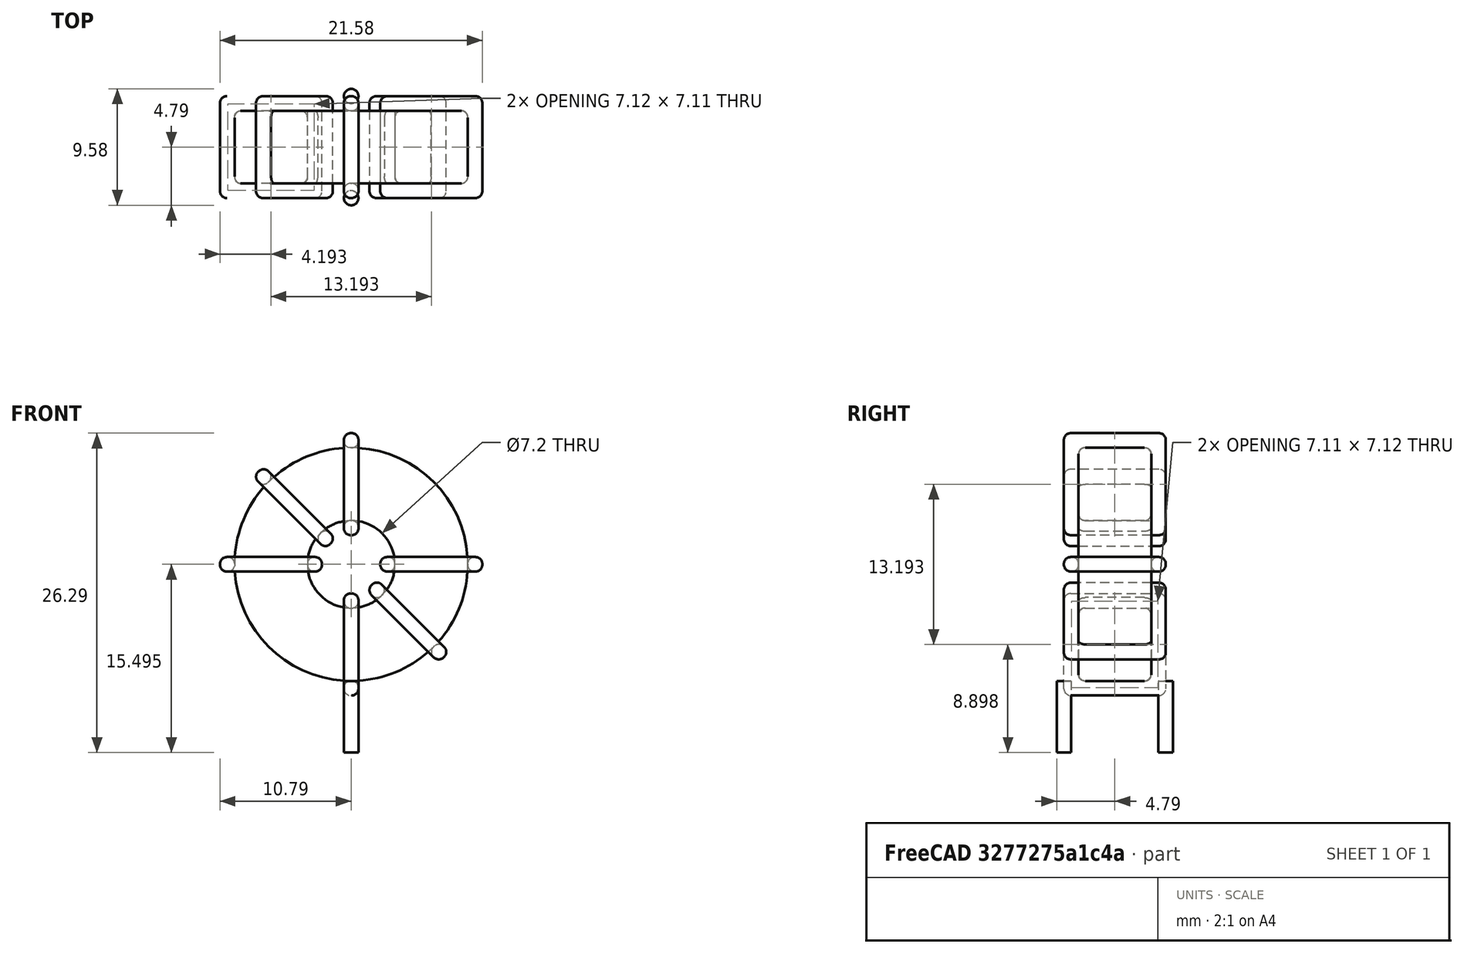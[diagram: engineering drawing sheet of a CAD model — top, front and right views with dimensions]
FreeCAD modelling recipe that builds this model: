
FCSTD DOCUMENT  (FreeCAD 0.16R6703 (Git))
Label: L_Toroid_Vertical_L21.6mm_W8.4mm_P8.38mm_Pulse_G
License: All rights reserved
LicenseURL: http://en.wikipedia.org/wiki/All_rights_reserved
objects: Sketcher::SketchObject×6, PartDesign::Pad×6, PartDesign::Fillet×5, Spreadsheet::Sheet×1
note: 23 computed .brp shape members not serialized (recipe doc carries the construction recipe); baked Part::Feature solids carry a one-line shape summary decoded from their .brp

FEATURE [Spreadsheet::Sheet] Spreadsheet  label="dimensions"
  cells = A1=Wx; B1(Wx)=21.59; C1(WW)=7.196666666666666; D1=21.59; A2=Wy; B2(Wy)=8.380000000000001; D2=8.380000000000001; A3=RM; B3(RMx)=8.380000000000001; C3(RMy)=0; A4=d_wire; B4(d_wire)=1.2; A5=H; B5(H)=21.59; A6=offsetx; B6(offsetx)=10.795
FEATURE [Sketcher::SketchObject] Sketch
  Placement = pos=(0,-4.19,0) rot=(1,0,0;1.5708rad)
  expr: Placement.Base.y = -Spreadsheet.RMx / 2
  expr: Constraints[0] = Spreadsheet.Wx / 2 - Spreadsheet.d_wire
  expr: Constraints[4] = Spreadsheet.WW / 2
  expr: Constraints[2] = Spreadsheet.Wx / 2 + Spreadsheet.d_wire + 0.5
  sketch-geometry (2):
    g0: Circle CenterX=0 CenterY=12.495 CenterZ=0 NormalX=0 NormalY=0 NormalZ=1 Radius=9.595
    g1: Circle CenterX=0 CenterY=12.495 CenterZ=0 NormalX=0 NormalY=0 NormalZ=1 Radius=3.59833
  constraints (5):
    c: Radius(g0) = 9.595
    c: DistanceX(g-1,g0) = 0
    c: DistanceY(g-1,g0) = 12.495
    c: Coincident(g1,g0)
    c: Radius(g1) = 3.59833
FEATURE [PartDesign::Pad] Pad
  Length = 5.98
  Length2 = 100
  Midplane = true
  Placement = pos=(0,-4.19,0) rot=(1,0,0;1.5708rad)
  Sketch = -> Sketch
  Type = 0
  expr: Length = Spreadsheet.Wy - 2 * Spreadsheet.d_wire
FEATURE [Sketcher::SketchObject] Sketch001
  Placement = pos=(0,0,1.7) rot=(0,0,1;0rad)
  expr: Placement.Base.z = 0.5 + Spreadsheet.d_wire
  expr: Constraints[4] = Spreadsheet.RMy
  expr: Constraints[2] = -Spreadsheet.RMx
  expr: Constraints[1] = Spreadsheet.d_wire / 2
  sketch-geometry (2):
    g0: Circle CenterX=0 CenterY=0 CenterZ=0 NormalX=0 NormalY=0 NormalZ=1 Radius=0.6
    g1: Circle CenterX=0 CenterY=-8.38 CenterZ=0 NormalX=0 NormalY=0 NormalZ=1 Radius=0.6
  constraints (5):
    c: Equal(g0,g1)
    c: Radius(g0) = 0.6
    c: DistanceY(g-1,g1) = -8.38
    c: Coincident(g0,g-1)
    c: DistanceX(g-1,g1) = 0
FEATURE [PartDesign::Pad] Pad001
  Length = 1.2
  Length2 = 4.7
  Placement = pos=(0,0,1.7) rot=(0,0,1;0rad)
  Reversed = true
  Sketch = -> Sketch001
  Type = 4
  expr: Length2 = 3.5 + Spreadsheet.d_wire
  expr: Length = Spreadsheet.d_wire
FEATURE [PartDesign::Fillet] Fillet
  Base = -> Pad [Edge6,Edge3,Edge2]
  Placement = pos=(0,-4.19,0) rot=(1,0,0;1.5708rad)
  Radius = 0.5
FEATURE [Sketcher::SketchObject] Sketch003
  Placement = pos=(0,0,12.495) rot=(1,0,0;3.14159rad)
  expr: Constraints[18] = Spreadsheet.d_wire
  expr: Constraints[16] = Spreadsheet.d_wire
  expr: Constraints[19] = Spreadsheet.d_wire
  expr: Constraints[17] = Spreadsheet.d_wire
  expr: Placement.Base.y = -1 * (Spreadsheet.RMx - Spreadsheet.Wy) / 2
  expr: Constraints[21] = (Spreadsheet.Wx - Spreadsheet.WW) / 2 - Spreadsheet.d_wire
  expr: Constraints[22] = Spreadsheet.Wx / 2 - Spreadsheet.d_wire
  expr: Constraints[43] = Spreadsheet.d_wire
  expr: Constraints[48] = Spreadsheet.Wx - Spreadsheet.d_wire * 2
  expr: Constraints[49] = Spreadsheet.Wy
  expr: Placement.Base.z = Spreadsheet.Wx / 2 + Spreadsheet.d_wire + 0.5
  sketch-geometry (16):
    g0: LineSegment StartX=-2.39833 StartY=0 StartZ=0 EndX=-10.795 EndY=0 EndZ=0
    g1: LineSegment StartX=-10.795 StartY=0 StartZ=0 EndX=-10.795 EndY=8.38 EndZ=0
    g2: LineSegment StartX=-10.795 StartY=8.38 StartZ=0 EndX=-2.39833 EndY=8.38 EndZ=0
    g3: LineSegment StartX=-2.39833 StartY=8.38 StartZ=0 EndX=-2.39833 EndY=0 EndZ=0
    g4: LineSegment StartX=-9.595 StartY=7.18 StartZ=0 EndX=-3.59833 EndY=7.18 EndZ=0
    g5: LineSegment StartX=-3.59833 StartY=7.18 StartZ=0 EndX=-3.59833 EndY=1.2 EndZ=0
    g6: LineSegment StartX=-3.59833 StartY=1.2 StartZ=0 EndX=-9.595 EndY=1.2 EndZ=0
    g7: LineSegment StartX=-9.595 StartY=1.2 StartZ=0 EndX=-9.595 EndY=7.18 EndZ=0
    g8: LineSegment StartX=2.39833 StartY=8.38 StartZ=0 EndX=10.795 EndY=8.38 EndZ=0
    g9: LineSegment StartX=10.795 StartY=8.38 StartZ=0 EndX=10.795 EndY=0 EndZ=0
    g10: LineSegment StartX=10.795 StartY=0 StartZ=0 EndX=2.39833 EndY=0 EndZ=0
    g11: LineSegment StartX=2.39833 StartY=0 StartZ=0 EndX=2.39833 EndY=8.38 EndZ=0
    g12: LineSegment StartX=3.59833 StartY=7.18 StartZ=0 EndX=9.595 EndY=7.18 EndZ=0
    g13: LineSegment StartX=9.595 StartY=7.18 StartZ=0 EndX=9.595 EndY=1.2 EndZ=0
    g14: LineSegment StartX=9.595 StartY=1.2 StartZ=0 EndX=3.59833 EndY=1.2 EndZ=0
    g15: LineSegment StartX=3.59833 StartY=1.2 StartZ=0 EndX=3.59833 EndY=7.18 EndZ=0
  constraints (50):
    c: Horizontal(g0)
    c: Coincident(g1,g0)
    c: Vertical(g1)
    c: Coincident(g2,g1)
    c: Horizontal(g2)
    c: Coincident(g3,g2)
    c: Coincident(g3,g0)
    c: Vertical(g3)
    c: Coincident(g4,g5)
    c: Coincident(g5,g6)
    c: Coincident(g6,g7)
    c: Coincident(g7,g4)
    c: Horizontal(g4)
    c: Horizontal(g6)
    c: Vertical(g5)
    c: Vertical(g7)
    c: DistanceX(g1,g4) = 1.2
    c: DistanceY(g4,g1) = 1.2
    c: DistanceX(g5,g0) = 1.2
    c: DistanceY(g0,g5) = 1.2
    c: DistanceY(g-1,g0) = 0
    c: DistanceX(g6,g6) = 5.99667
    c: DistanceX(g6,g-1) = 9.595
    c: Coincident(g8,g9)
    c: Coincident(g9,g10)
    c: Coincident(g10,g11)
    c: Coincident(g11,g8)
    c: Horizontal(g8)
    c: Horizontal(g10)
    c: Vertical(g9)
    c: Vertical(g11)
    c: Coincident(g12,g13)
    c: Coincident(g13,g14)
    c: Coincident(g14,g15)
    c: Coincident(g15,g12)
    c: Horizontal(g12)
    c: Horizontal(g14)
    c: Vertical(g13)
    c: Vertical(g15)
    c: DistanceY(g8,g2) = 0
    c: DistanceY(g10,g0) = 0
    c: DistanceY(g14,g5) = 0
    c: DistanceY(g12,g4) = 0
    c: DistanceX(g8,g12) = 1.2
    c: Equal(g8,g2)
    c: Equal(g12,g4)
    c: Equal(g9,g1)
    c: Equal(g13,g7)
    c: DistanceX(g4,g12) = 19.19
    c: DistanceY(g0,g1) = 8.38
FEATURE [PartDesign::Pad] Pad002
  Length = 1.2
  Length2 = 100
  Midplane = true
  Placement = pos=(0,0,12.495) rot=(1,0,0;3.14159rad)
  Sketch = -> Sketch003
  Type = 0
  expr: Length = Spreadsheet.d_wire
FEATURE [PartDesign::Fillet] Fillet001
  Base = -> Pad002 [Edge38,Edge41,Edge42,Edge43,Edge29,Edge32,Edge33,Edge34,Edge25,Edge35,Edge36,Edge13,Edge14,Edge15,Edge16,Edge17,Edge18,Edge19,Edge1,Edge2,Edge3,Edge4,Edge5,Edge6,Edge7,Edge37,Edge39,Edge40,Edge20,Edge23,Edge24,Edge21,Edge22,Edge8,Edge9,Edge10,Edge11,Edge12,Edge26,Edge27,+8 more]
  Placement = pos=(0,0,12.495) rot=(1,0,0;3.14159rad)
  Radius = 0.564
  expr: Radius = Spreadsheet.d_wire * 0.47
FEATURE [Sketcher::SketchObject] Sketch004
  Placement = pos=(0,0,12.495) rot=(0.92388,0,0.382683;3.14159rad)
  expr: Constraints[18] = Spreadsheet.d_wire
  expr: Constraints[16] = Spreadsheet.d_wire
  expr: Constraints[19] = Spreadsheet.d_wire
  expr: Constraints[17] = Spreadsheet.d_wire
  expr: Placement.Base.y = -1 * (Spreadsheet.RMx - Spreadsheet.Wy) / 2
  expr: Constraints[21] = (Spreadsheet.Wx - Spreadsheet.WW) / 2 - Spreadsheet.d_wire
  expr: Constraints[22] = Spreadsheet.Wx / 2 - Spreadsheet.d_wire
  expr: Constraints[43] = Spreadsheet.d_wire
  expr: Constraints[48] = Spreadsheet.Wx - 2 * Spreadsheet.d_wire
  expr: Constraints[49] = Spreadsheet.Wy
  expr: Placement.Base.z = Spreadsheet.Wx / 2 + Spreadsheet.d_wire + 0.5
  sketch-geometry (16):
    g0: LineSegment StartX=-2.39833 StartY=0 StartZ=0 EndX=-10.795 EndY=0 EndZ=0
    g1: LineSegment StartX=-10.795 StartY=0 StartZ=0 EndX=-10.795 EndY=8.38 EndZ=0
    g2: LineSegment StartX=-10.795 StartY=8.38 StartZ=0 EndX=-2.39833 EndY=8.38 EndZ=0
    g3: LineSegment StartX=-2.39833 StartY=8.38 StartZ=0 EndX=-2.39833 EndY=0 EndZ=0
    g4: LineSegment StartX=-9.595 StartY=7.18 StartZ=0 EndX=-3.59833 EndY=7.18 EndZ=0
    g5: LineSegment StartX=-3.59833 StartY=7.18 StartZ=0 EndX=-3.59833 EndY=1.2 EndZ=0
    g6: LineSegment StartX=-3.59833 StartY=1.2 StartZ=0 EndX=-9.595 EndY=1.2 EndZ=0
    g7: LineSegment StartX=-9.595 StartY=1.2 StartZ=0 EndX=-9.595 EndY=7.18 EndZ=0
    g8: LineSegment StartX=2.39833 StartY=8.38 StartZ=0 EndX=10.795 EndY=8.38 EndZ=0
    g9: LineSegment StartX=10.795 StartY=8.38 StartZ=0 EndX=10.795 EndY=0 EndZ=0
    g10: LineSegment StartX=10.795 StartY=0 StartZ=0 EndX=2.39833 EndY=0 EndZ=0
    g11: LineSegment StartX=2.39833 StartY=0 StartZ=0 EndX=2.39833 EndY=8.38 EndZ=0
    g12: LineSegment StartX=3.59833 StartY=7.18 StartZ=0 EndX=9.595 EndY=7.18 EndZ=0
    g13: LineSegment StartX=9.595 StartY=7.18 StartZ=0 EndX=9.595 EndY=1.2 EndZ=0
    g14: LineSegment StartX=9.595 StartY=1.2 StartZ=0 EndX=3.59833 EndY=1.2 EndZ=0
    g15: LineSegment StartX=3.59833 StartY=1.2 StartZ=0 EndX=3.59833 EndY=7.18 EndZ=0
  constraints (50):
    c: Horizontal(g0)
    c: Coincident(g1,g0)
    c: Vertical(g1)
    c: Coincident(g2,g1)
    c: Horizontal(g2)
    c: Coincident(g3,g2)
    c: Coincident(g3,g0)
    c: Vertical(g3)
    c: Coincident(g4,g5)
    c: Coincident(g5,g6)
    c: Coincident(g6,g7)
    c: Coincident(g7,g4)
    c: Horizontal(g4)
    c: Horizontal(g6)
    c: Vertical(g5)
    c: Vertical(g7)
    c: DistanceX(g1,g4) = 1.2
    c: DistanceY(g4,g1) = 1.2
    c: DistanceX(g5,g0) = 1.2
    c: DistanceY(g0,g5) = 1.2
    c: DistanceY(g-1,g0) = 0
    c: DistanceX(g6,g6) = 5.99667
    c: DistanceX(g6,g-1) = 9.595
    c: Coincident(g8,g9)
    c: Coincident(g9,g10)
    c: Coincident(g10,g11)
    c: Coincident(g11,g8)
    c: Horizontal(g8)
    c: Horizontal(g10)
    c: Vertical(g9)
    c: Vertical(g11)
    c: Coincident(g12,g13)
    c: Coincident(g13,g14)
    c: Coincident(g14,g15)
    c: Coincident(g15,g12)
    c: Horizontal(g12)
    c: Horizontal(g14)
    c: Vertical(g13)
    c: Vertical(g15)
    c: DistanceY(g8,g2) = 0
    c: DistanceY(g10,g0) = 0
    c: DistanceY(g14,g5) = 0
    c: DistanceY(g12,g4) = 0
    c: DistanceX(g8,g12) = 1.2
    c: Equal(g8,g2)
    c: Equal(g12,g4)
    c: Equal(g9,g1)
    c: Equal(g13,g7)
    c: DistanceX(g4,g12) = 19.19
    c: DistanceY(g0,g1) = 8.38
FEATURE [PartDesign::Pad] Pad003
  Length = 1.2
  Length2 = 100
  Midplane = true
  Placement = pos=(0,0,12.495) rot=(0.92388,0,0.382683;3.14159rad)
  Sketch = -> Sketch004
  Type = 0
  expr: Length = Spreadsheet.d_wire
FEATURE [PartDesign::Fillet] Fillet002
  Base = -> Pad003 [Edge38,Edge41,Edge42,Edge43,Edge29,Edge32,Edge33,Edge34,Edge25,Edge35,Edge36,Edge13,Edge14,Edge15,Edge16,Edge17,Edge18,Edge19,Edge1,Edge2,Edge3,Edge4,Edge5,Edge6,Edge7,Edge37,Edge39,Edge40,Edge20,Edge23,Edge24,Edge21,Edge22,Edge8,Edge9,Edge10,Edge11,Edge12,Edge26,Edge27,+8 more]
  Placement = pos=(0,0,12.495) rot=(0.92388,0,0.382683;3.14159rad)
  Radius = 0.564
  expr: Radius = Spreadsheet.d_wire * 0.47
FEATURE [Sketcher::SketchObject] Sketch005
  Placement = pos=(0,0,12.495) rot=(0.92388,0,-0.382683;3.14159rad)
  expr: Constraints[18] = Spreadsheet.d_wire
  expr: Constraints[16] = Spreadsheet.d_wire
  expr: Constraints[19] = Spreadsheet.d_wire
  expr: Constraints[17] = Spreadsheet.d_wire
  expr: Placement.Base.y = -1 * (Spreadsheet.RMx - Spreadsheet.Wy) / 2
  expr: Constraints[21] = (Spreadsheet.Wx - Spreadsheet.WW) / 2 - Spreadsheet.d_wire
  expr: Constraints[22] = Spreadsheet.Wx / 2 - Spreadsheet.d_wire
  expr: Constraints[43] = Spreadsheet.d_wire
  expr: Constraints[48] = Spreadsheet.Wx - 2 * Spreadsheet.d_wire
  expr: Constraints[49] = Spreadsheet.Wy
  expr: Placement.Base.z = Spreadsheet.Wx / 2 + Spreadsheet.d_wire + 0.5
  sketch-geometry (16):
    g0: LineSegment StartX=-2.39833 StartY=0 StartZ=0 EndX=-10.795 EndY=0 EndZ=0
    g1: LineSegment StartX=-10.795 StartY=0 StartZ=0 EndX=-10.795 EndY=8.38 EndZ=0
    g2: LineSegment StartX=-10.795 StartY=8.38 StartZ=0 EndX=-2.39833 EndY=8.38 EndZ=0
    g3: LineSegment StartX=-2.39833 StartY=8.38 StartZ=0 EndX=-2.39833 EndY=0 EndZ=0
    g4: LineSegment StartX=-9.595 StartY=7.18 StartZ=0 EndX=-3.59833 EndY=7.18 EndZ=0
    g5: LineSegment StartX=-3.59833 StartY=7.18 StartZ=0 EndX=-3.59833 EndY=1.2 EndZ=0
    g6: LineSegment StartX=-3.59833 StartY=1.2 StartZ=0 EndX=-9.595 EndY=1.2 EndZ=0
    g7: LineSegment StartX=-9.595 StartY=1.2 StartZ=0 EndX=-9.595 EndY=7.18 EndZ=0
    g8: LineSegment StartX=2.39833 StartY=8.38 StartZ=0 EndX=10.795 EndY=8.38 EndZ=0
    g9: LineSegment StartX=10.795 StartY=8.38 StartZ=0 EndX=10.795 EndY=0 EndZ=0
    g10: LineSegment StartX=10.795 StartY=0 StartZ=0 EndX=2.39833 EndY=0 EndZ=0
    g11: LineSegment StartX=2.39833 StartY=0 StartZ=0 EndX=2.39833 EndY=8.38 EndZ=0
    g12: LineSegment StartX=3.59833 StartY=7.18 StartZ=0 EndX=9.595 EndY=7.18 EndZ=0
    g13: LineSegment StartX=9.595 StartY=7.18 StartZ=0 EndX=9.595 EndY=1.2 EndZ=0
    g14: LineSegment StartX=9.595 StartY=1.2 StartZ=0 EndX=3.59833 EndY=1.2 EndZ=0
    g15: LineSegment StartX=3.59833 StartY=1.2 StartZ=0 EndX=3.59833 EndY=7.18 EndZ=0
  constraints (50):
    c: Horizontal(g0)
    c: Coincident(g1,g0)
    c: Vertical(g1)
    c: Coincident(g2,g1)
    c: Horizontal(g2)
    c: Coincident(g3,g2)
    c: Coincident(g3,g0)
    c: Vertical(g3)
    c: Coincident(g4,g5)
    c: Coincident(g5,g6)
    c: Coincident(g6,g7)
    c: Coincident(g7,g4)
    c: Horizontal(g4)
    c: Horizontal(g6)
    c: Vertical(g5)
    c: Vertical(g7)
    c: DistanceX(g1,g4) = 1.2
    c: DistanceY(g4,g1) = 1.2
    c: DistanceX(g5,g0) = 1.2
    c: DistanceY(g0,g5) = 1.2
    c: DistanceY(g-1,g0) = 0
    c: DistanceX(g6,g6) = 5.99667
    c: DistanceX(g6,g-1) = 9.595
    c: Coincident(g8,g9)
    c: Coincident(g9,g10)
    c: Coincident(g10,g11)
    c: Coincident(g11,g8)
    c: Horizontal(g8)
    c: Horizontal(g10)
    c: Vertical(g9)
    c: Vertical(g11)
    c: Coincident(g12,g13)
    c: Coincident(g13,g14)
    c: Coincident(g14,g15)
    c: Coincident(g15,g12)
    c: Horizontal(g12)
    c: Horizontal(g14)
    c: Vertical(g13)
    c: Vertical(g15)
    c: DistanceY(g8,g2) = 0
    c: DistanceY(g10,g0) = 0
    c: DistanceY(g14,g5) = 0
    c: DistanceY(g12,g4) = 0
    c: DistanceX(g8,g12) = 1.2
    c: Equal(g8,g2)
    c: Equal(g12,g4)
    c: Equal(g9,g1)
    c: Equal(g13,g7)
    c: DistanceX(g4,g12) = 19.19
    c: DistanceY(g0,g1) = 8.38
FEATURE [PartDesign::Pad] Pad004
  Length = 1.2
  Length2 = 100
  Midplane = true
  Placement = pos=(0,0,12.495) rot=(0.92388,0,-0.382683;3.14159rad)
  Sketch = -> Sketch005
  Type = 0
  expr: Length = Spreadsheet.d_wire
FEATURE [PartDesign::Fillet] Fillet003
  Base = -> Pad004 [Edge38,Edge41,Edge42,Edge43,Edge29,Edge32,Edge33,Edge34,Edge25,Edge35,Edge36,Edge13,Edge14,Edge15,Edge16,Edge17,Edge18,Edge19,Edge1,Edge2,Edge3,Edge4,Edge5,Edge6,Edge7,Edge37,Edge39,Edge40,Edge20,Edge23,Edge24,Edge21,Edge22,Edge8,Edge9,Edge10,Edge11,Edge12,Edge26,Edge27,+8 more]
  Placement = pos=(0,0,12.495) rot=(0.92388,0,-0.382683;3.14159rad)
  Radius = 0.564
  expr: Radius = Spreadsheet.d_wire * 0.47
FEATURE [Sketcher::SketchObject] Sketch006
  Placement = pos=(0,0,12.495) rot=(0.707107,0,0.707107;3.14159rad)
  expr: Constraints[18] = Spreadsheet.d_wire
  expr: Constraints[16] = Spreadsheet.d_wire
  expr: Constraints[19] = Spreadsheet.d_wire
  expr: Constraints[17] = Spreadsheet.d_wire
  expr: Placement.Base.y = -1 * (Spreadsheet.RMx - Spreadsheet.Wy) / 2
  expr: Constraints[21] = (Spreadsheet.Wx - Spreadsheet.WW) / 2 - Spreadsheet.d_wire
  expr: Constraints[22] = Spreadsheet.Wx / 2 - Spreadsheet.d_wire
  expr: Constraints[43] = Spreadsheet.d_wire
  expr: Constraints[48] = Spreadsheet.Wx - Spreadsheet.d_wire * 2
  expr: Constraints[49] = Spreadsheet.Wy
  expr: Placement.Base.z = Spreadsheet.Wx / 2 + Spreadsheet.d_wire + 0.5
  sketch-geometry (16):
    g0: LineSegment StartX=-2.39833 StartY=0 StartZ=0 EndX=-10.795 EndY=0 EndZ=0
    g1: LineSegment StartX=-10.795 StartY=0 StartZ=0 EndX=-10.795 EndY=8.38 EndZ=0
    g2: LineSegment StartX=-10.795 StartY=8.38 StartZ=0 EndX=-2.39833 EndY=8.38 EndZ=0
    g3: LineSegment StartX=-2.39833 StartY=8.38 StartZ=0 EndX=-2.39833 EndY=0 EndZ=0
    g4: LineSegment StartX=-9.595 StartY=7.18 StartZ=0 EndX=-3.59833 EndY=7.18 EndZ=0
    g5: LineSegment StartX=-3.59833 StartY=7.18 StartZ=0 EndX=-3.59833 EndY=1.2 EndZ=0
    g6: LineSegment StartX=-3.59833 StartY=1.2 StartZ=0 EndX=-9.595 EndY=1.2 EndZ=0
    g7: LineSegment StartX=-9.595 StartY=1.2 StartZ=0 EndX=-9.595 EndY=7.18 EndZ=0
    g8: LineSegment StartX=2.39833 StartY=8.38 StartZ=0 EndX=10.795 EndY=8.38 EndZ=0
    g9: LineSegment StartX=10.795 StartY=8.38 StartZ=0 EndX=10.795 EndY=0 EndZ=0
    g10: LineSegment StartX=10.795 StartY=0 StartZ=0 EndX=2.39833 EndY=0 EndZ=0
    g11: LineSegment StartX=2.39833 StartY=0 StartZ=0 EndX=2.39833 EndY=8.38 EndZ=0
    g12: LineSegment StartX=3.59833 StartY=7.18 StartZ=0 EndX=9.595 EndY=7.18 EndZ=0
    g13: LineSegment StartX=9.595 StartY=7.18 StartZ=0 EndX=9.595 EndY=1.2 EndZ=0
    g14: LineSegment StartX=9.595 StartY=1.2 StartZ=0 EndX=3.59833 EndY=1.2 EndZ=0
    g15: LineSegment StartX=3.59833 StartY=1.2 StartZ=0 EndX=3.59833 EndY=7.18 EndZ=0
  constraints (50):
    c: Horizontal(g0)
    c: Coincident(g1,g0)
    c: Vertical(g1)
    c: Coincident(g2,g1)
    c: Horizontal(g2)
    c: Coincident(g3,g2)
    c: Coincident(g3,g0)
    c: Vertical(g3)
    c: Coincident(g4,g5)
    c: Coincident(g5,g6)
    c: Coincident(g6,g7)
    c: Coincident(g7,g4)
    c: Horizontal(g4)
    c: Horizontal(g6)
    c: Vertical(g5)
    c: Vertical(g7)
    c: DistanceX(g1,g4) = 1.2
    c: DistanceY(g4,g1) = 1.2
    c: DistanceX(g5,g0) = 1.2
    c: DistanceY(g0,g5) = 1.2
    c: DistanceY(g-1,g0) = 0
    c: DistanceX(g6,g6) = 5.99667
    c: DistanceX(g6,g-1) = 9.595
    c: Coincident(g8,g9)
    c: Coincident(g9,g10)
    c: Coincident(g10,g11)
    c: Coincident(g11,g8)
    c: Horizontal(g8)
    c: Horizontal(g10)
    c: Vertical(g9)
    c: Vertical(g11)
    c: Coincident(g12,g13)
    c: Coincident(g13,g14)
    c: Coincident(g14,g15)
    c: Coincident(g15,g12)
    c: Horizontal(g12)
    c: Horizontal(g14)
    c: Vertical(g13)
    c: Vertical(g15)
    c: DistanceY(g8,g2) = 0
    c: DistanceY(g10,g0) = 0
    c: DistanceY(g14,g5) = 0
    c: DistanceY(g12,g4) = 0
    c: DistanceX(g8,g12) = 1.2
    c: Equal(g8,g2)
    c: Equal(g12,g4)
    c: Equal(g9,g1)
    c: Equal(g13,g7)
    c: DistanceX(g4,g12) = 19.19
    c: DistanceY(g0,g1) = 8.38
FEATURE [PartDesign::Pad] Pad005
  Length = 1.2
  Length2 = 100
  Midplane = true
  Placement = pos=(0,0,12.495) rot=(0.707107,0,0.707107;3.14159rad)
  Sketch = -> Sketch006
  Type = 0
  expr: Length = Spreadsheet.d_wire
FEATURE [PartDesign::Fillet] Fillet004
  Base = -> Pad005 [Edge38,Edge41,Edge42,Edge43,Edge29,Edge32,Edge33,Edge34,Edge25,Edge35,Edge36,Edge13,Edge14,Edge15,Edge16,Edge17,Edge18,Edge19,Edge1,Edge2,Edge3,Edge4,Edge5,Edge6,Edge7,Edge37,Edge39,Edge40,Edge20,Edge23,Edge24,Edge21,Edge22,Edge8,Edge9,Edge10,Edge11,Edge12,Edge26,Edge27,+8 more]
  Placement = pos=(0,0,12.495) rot=(0.707107,0,0.707107;3.14159rad)
  Radius = 0.564
  expr: Radius = Spreadsheet.d_wire * 0.47
